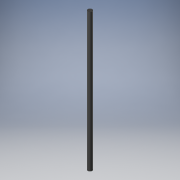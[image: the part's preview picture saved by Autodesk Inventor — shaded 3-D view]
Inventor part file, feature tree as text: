
AUTODESK INVENTOR PART (.ipt)
format: ipt  version: 2019 (Build 230136000, 136)  size: 89,600 bytes
history: native  units: in
note: dims shown in document units (in); Inventor stores cm internally (conversion verified against a paired STEP export)
features: extrude x1, sketch x1
ambient origin geometry x8: Origin, YZ Plane, XZ Plane, XY Plane, X Axis, Y Axis, Z Axis, Center Point
bodies: Solid1 (feature_tree)
feature tree (2):
  extrude  "Extrusion1"  Depth=8.375in TaperAngle=0.0deg
  sketch  "Sketch1"  dims[d0=0.25in d1=8.375in d2=0.0in]
